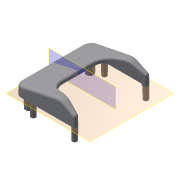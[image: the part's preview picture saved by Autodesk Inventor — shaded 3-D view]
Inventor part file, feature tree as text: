
AUTODESK INVENTOR PART (.ipt)
format: ipt  version: 2016 (Build 200138000, 138)  size: 471,040 bytes
history: native  units: mm
features: extrude x9, sketch x9, fillet x6, projected_geometry x6, reference x3, plane x2, shell x1
ambient origin geometry x8: Origin, YZ Plane, XZ Plane, XY Plane, X Axis, Y Axis, Z Axis, Center Point
bodies: Solid1 (feature_tree)
feature tree (36):
  plane  "Work Plane1"
  extrude  "Extrusion1"  Depth=1.0mm
  fillet  "Fillet1"  Radius=3.0mm
  plane  "Work Plane2"
  extrude  "Extrusion2"  Depth=5.0mm
  fillet  "Fillet2"  Radius=1.0mm
  fillet  "Fillet3"  Radius=1.5mm
  shell  "Shell1"  Thickness=3.05mm
  extrude  "Extrusion3"  Depth=0.174533mm
  fillet  "Fillet4"  Radius=1.0mm
  extrude  "Extrusion4"  Depth=3.05mm
  extrude  "Extrusion5"  TaperAngle=15.0deg  [1 undecoded]
  fillet  "Fillet5"  [1 undecoded]
  fillet  "Fillet6"  Radius=12.0mm
  extrude  "Extrusion6"  Depth=5.0mm
  extrude  "Extrusion7"  Depth=0.349066mm TaperAngle=0.0deg
  extrude  "Extrusion8"  Depth=5.0mm
  extrude  "Extrusion9"  Depth=5.0mm
  sketch  "Sketch1"  dims[d1=1.0mm d2=7.0mm d3=-0.349066mm d4=3.0mm]
  reference  "Reference1"
  sketch  "Sketch2"  dims[d5=60.0mm d6=0.0mm d7=5.0mm d8=1.0mm d9=1.5mm d10=3.05mm]
  sketch  "Sketch3"  dims[d11=3.05mm d12=60.0mm d13=0.174533mm d14=1.0mm]
  projected_geometry  "Projected Loop1"
  sketch  "Sketch4"  dims[d15=3.05mm d16=3.05mm]
  projected_geometry  "Projected Loop2"
  sketch  "Sketch5"  dims[d17=7.0mm d18=-0.087266mm d19=15.0deg d20=15.0deg d21=12.0mm]
  projected_geometry  "Projected Loop3"
  sketch  "Sketch6"  dims[d22=10.0mm d23=0.349066mm d24=5.0mm]
  projected_geometry  "Projected Loop4"
  sketch  "Sketch7"  dims[d25=0.7mm d27=0.0mm d28=0.349066mm]
  projected_geometry  "Projected Loop5"
  sketch  "Sketch8"  dims[d29=5.0mm d30=-0.174533mm d31=2.0mm]
  reference  "Reference2"
  reference  "Reference3"
  sketch  "Sketch9"  dims[d32=16.3mm d33=2.0mm d34=0.0mm d35=0.0mm d36=0.174533mm d37=5.0mm d38=-0.174533mm]
  projected_geometry  "Projected Loop6"
note: 2 required parameter values undecoded (feature->parameter linkage not recoverable at this tier; creation-order binding heuristic only, values carry confidence <= 0.55)
